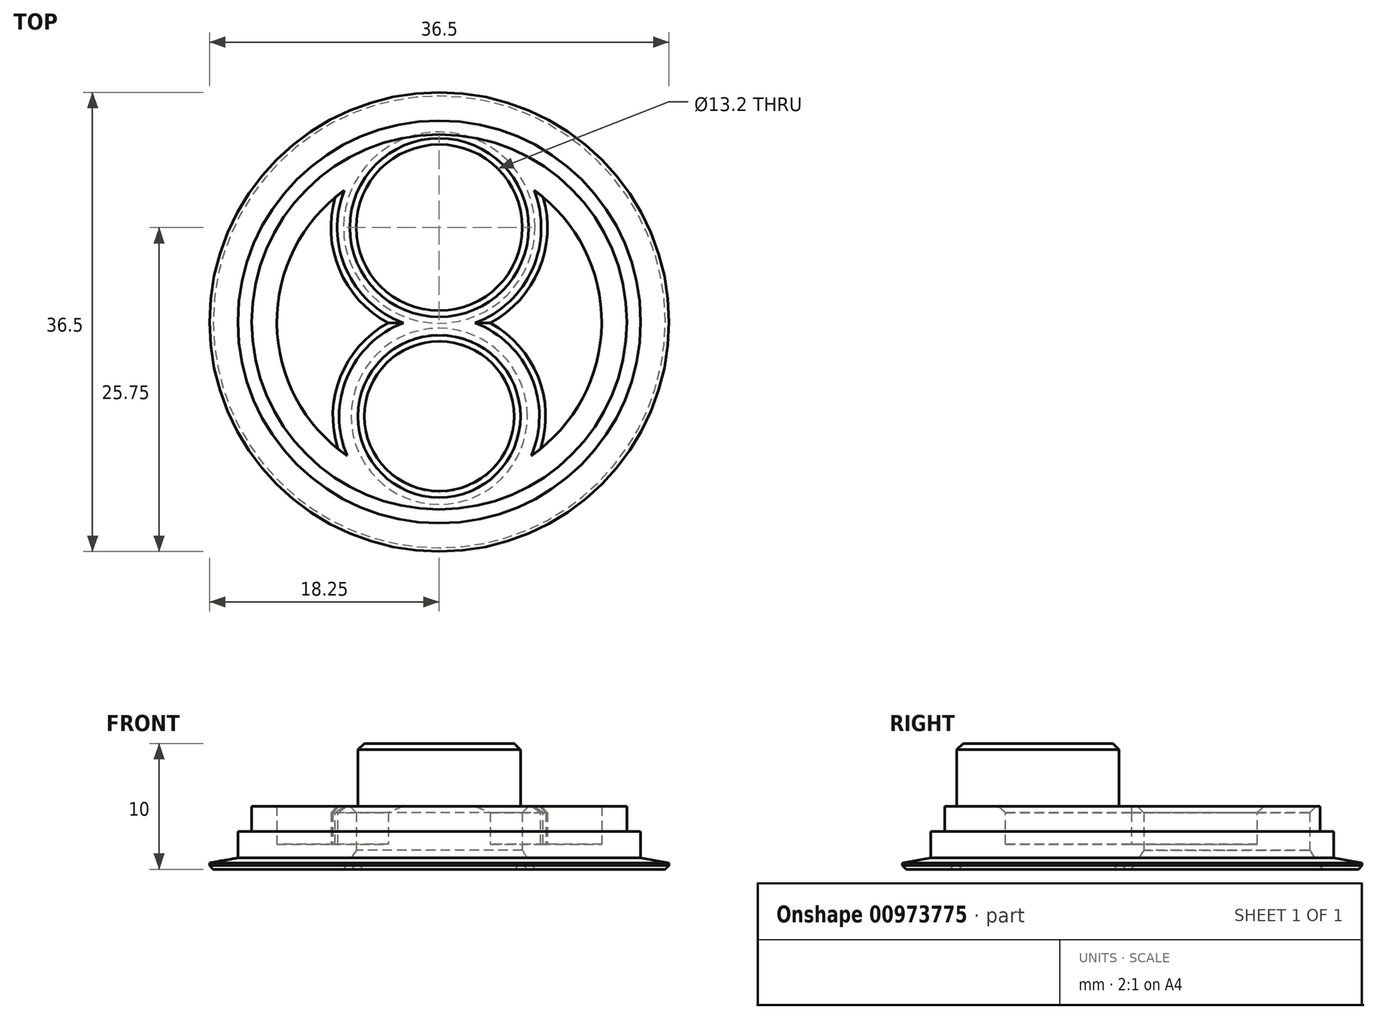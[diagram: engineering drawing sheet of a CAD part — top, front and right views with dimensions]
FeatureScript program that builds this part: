
annotation { "Feature Type Name" : "Feature", "Feature Type Description" : "" }
export const myFeature = defineFeature(function(context is Context, id is Id, definition is map)
    precondition{}
    {
        {
            var Q0;
            Q0=qCreatedBy(makeId("Top.planeOp"),FACE);
            var sketch = newSketch(context, id + "F0", { "sketchPlane" : qUnion([Q0])});
            skCircle(sketch, "E0", {"center": v(0, 0) * mm, "radius": 14.9 * mm});
            skCircle(sketch, "E1", {"center": v(0, 0) * mm, "radius": 18.25 * mm});
            skCircle(sketch, "E2", {"center": v(0, -7.5) * mm, "radius": 6.6 * mm});
            skCircle(sketch, "E3", {"center": v(0, 7.5) * mm, "radius": 6.6 * mm});
            skCircle(sketch, "E4", {"center": v(0, 0) * mm, "radius": 16 * mm});
            skSolve(sketch);
        }
        {
            var Q0;
            Q0=makeQuery(id+"F0.imprint","IMPRINT",FACE,{"disambiguationData":[TD([[makeQuery(id+"F0.imprint","IMPRINT",EDGE,{"derivedFrom":sQuery(id+"F0.wireOp",EDGE,"E0")}),1.0]])]});
            extrude(context, id + "F1", {"entities" : qUnion([Q0]), "depth" : 5 * mm, "offsetDistance" : 25 * mm});
        }
        {
            var Q0;
            Q0=makeQuery(id+"F1.opExtrude","CAP_FACE",FACE,{"disambiguationData":[OSD([sQuery(id+"F0.wireOp",EDGE,"E0"),sQuery(id+"F0.wireOp",EDGE,"E2")])],"isStart":false});
            shell(context, id + "F2", {"entities" : qUnion([Q0]), "thickness" : 2 * mm});
        }
        {
            var Q0;
            Q0=makeQuery(id+"F0.imprint","IMPRINT",FACE,{"disambiguationData":[TD([[makeQuery(id+"F0.imprint","IMPRINT",EDGE,{"derivedFrom":sQuery(id+"F0.wireOp",EDGE,"E0")}),-1.0]])]});
            extrude(context, id + "F3", {"entities" : qUnion([Q0]), "operationType" : NewBodyOperationType.ADD, "depth" : 3 * mm, "offsetDistance" : 25 * mm});
        }
        {
            var Q0;
            Q0 = qSketchRegion(id + "F0", true);
            extrude(context, id + "F4", {"entities" : qUnion([Q0]), "operationType" : NewBodyOperationType.ADD, "depth" : 1 * mm, "offsetDistance" : 25 * mm});
        }
        {
            var Q0;
            Q0=makeQuery(id+"F4.opExtrude","CAP_EDGE",EDGE,{"disambiguationData":[OSD([sQuery(id+"F0.wireOp",EDGE,"E1")])],"isStart":true});
            chamfer(context, id + "F5", {"entities" : qUnion([Q0]), "width" : 0.3 * mm, "tangentPropagation" : true});
        }
        {
            var Q0;
            Q0=makeQuery(id+"F1.opExtrude","SWEPT_FACE",FACE,{"disambiguationData":[OSD([sQuery(id+"F0.wireOp",EDGE,"E3")])]});
            var Q1;
            Q1=makeQuery(id+"F1.opExtrude","CAP_EDGE",EDGE,{"disambiguationData":[OSD([sQuery(id+"F0.wireOp",EDGE,"E2")])],"isStart":false});
            chamfer(context, id + "F6", {"entities" : qUnion([Q0, Q1]), "width" : .5 * mm, "tangentPropagation" : true});
        }
        {
            var Q0;
            Q0=makeQuery(id+"F1.opExtrude","CAP_EDGE",EDGE,{"disambiguationData":[OSD([sQuery(id+"F0.wireOp",EDGE,"E2")])],"isStart":true});
            chamfer(context, id + "F7", {"entities" : qUnion([Q0]), "chamferType" : ChamferType.TWO_OFFSETS, "width1" : 1 * mm, "oppositeDirection" : false, "width2" : 1.5 * mm, "tangentPropagation" : true});
        }
        {
            var Q0;
            Q0=makeQuery(id+"F4.opExtrude","CAP_EDGE",EDGE,{"disambiguationData":[OSD([sQuery(id+"F0.wireOp",EDGE,"E1")])],"isStart":false});
            chamfer(context, id + "F8", {"entities" : qUnion([Q0]), "chamferType" : ChamferType.TWO_OFFSETS, "width1" : 2.8 * mm, "oppositeDirection" : false, "width2" : .5 * mm, "tangentPropagation" : true});
        }
        {
            var Q0;
            Q0=qCreatedBy(makeId("Top.planeOp"),FACE);
            var sketch = newSketch(context, id + "F9", { "sketchPlane" : qUnion([Q0])});
            skCircle(sketch, "E5", {"center": v(0, 0) * mm, "radius": 14.9 * mm});
            skCircle(sketch, "E6", {"center": v(0, 0) * mm, "radius": 18.25 * mm});
            skCircle(sketch, "E7", {"center": v(0, -7.5) * mm, "radius": 6.45 * mm});
            skCircle(sketch, "E8", {"center": v(0, 7.5) * mm, "radius": 6.6 * mm});
            skCircle(sketch, "E9", {"center": v(0, 0) * mm, "radius": 16 * mm});
            skSolve(sketch);
        }
        {
            var Q0;
            Q0=makeQuery(id+"F9.imprint","IMPRINT",FACE,{"disambiguationData":[TD([[makeQuery(id+"F9.imprint","IMPRINT",EDGE,{"derivedFrom":sQuery(id+"F9.wireOp",EDGE,"E5")}),1.0]])]});
            extrude(context, id + "F10", {"entities" : qUnion([Q0]), "depth" : 5 * mm, "offsetDistance" : 25 * mm});
        }
        {
            var Q0;
            Q0=makeQuery(id+"F9.imprint","IMPRINT",FACE,{"disambiguationData":[TD([[makeQuery(id+"F9.imprint","IMPRINT",EDGE,{"derivedFrom":sQuery(id+"F9.wireOp",EDGE,"E5")}),-1.0]])]});
            extrude(context, id + "F11", {"entities" : qUnion([Q0]), "operationType" : NewBodyOperationType.ADD, "depth" : 3 * mm, "offsetDistance" : 25 * mm});
        }
        {
            var Q0;
            Q0=makeQuery(id+"F9.imprint","IMPRINT",FACE,{"disambiguationData":[TD([[makeQuery(id+"F9.imprint","IMPRINT",EDGE,{"derivedFrom":sQuery(id+"F9.wireOp",EDGE,"E6")}),1.0]])]});
            extrude(context, id + "F12", {"entities" : qUnion([Q0]), "operationType" : NewBodyOperationType.ADD, "depth" : 1 * mm, "offsetDistance" : 25 * mm});
        }
        {
            var Q0;
            Q0=makeQuery(id+"F10.opExtrude","CAP_FACE",FACE,{"disambiguationData":[OSD([sQuery(id+"F9.wireOp",EDGE,"E5"),sQuery(id+"F9.wireOp",EDGE,"E7"),sQuery(id+"F9.wireOp",EDGE,"E8")])],"isStart":false});
            shell(context, id + "F13", {"entities" : qUnion([Q0]), "thickness" : 2 * mm});
        }
        {
            var Q0;
            Q0=makeQuery(id+"F9.imprint","IMPRINT",FACE,{"disambiguationData":[TD([[makeQuery(id+"F9.imprint","IMPRINT",EDGE,{"derivedFrom":sQuery(id+"F9.wireOp",EDGE,"E7")}),1.0]])]});
            extrude(context, id + "F14", {"entities" : qUnion([Q0]), "operationType" : NewBodyOperationType.ADD, "depth" : 10 * mm, "offsetDistance" : 25 * mm});
        }
        {
            var Q0;
            Q0=makeQuery(id+"F14.opExtrude","CAP_EDGE",EDGE,{"disambiguationData":[OSD([sQuery(id+"F9.wireOp",EDGE,"E7")])],"isStart":false});
            var Q1;
            Q1=makeQuery(id+"F13.opShell","OFFSET_EDGE",EDGE,{"disambiguationData":[OSD([sQuery(id+"F9.wireOp",EDGE,"E5")]),OD(0.0)]});
            var Q2;
            {var subQ0=sQuery(id+"F9.wireOp",EDGE,"E7");Q2=makeQuery(id+"F13.opShell","OFFSET_EDGE",EDGE,{"disambiguationData":[OSD([subQ0]),TDD([makeQuery(id+"F10.opExtrude","CAP_EDGE",EDGE,{"disambiguationData":[OSD([subQ0])],"isStart":false})]),OD(0.0)]});}
            var Q3;
            {var subQ0=sQuery(id+"F9.wireOp",EDGE,"E8");Q3=makeQuery(id+"F13.opShell","OFFSET_EDGE",EDGE,{"disambiguationData":[OSD([subQ0]),TDD([makeQuery(id+"F10.opExtrude","CAP_EDGE",EDGE,{"disambiguationData":[OSD([subQ0])],"isStart":false})]),OD(0.0)]});}
            var Q4;
            {var subQ0=sQuery(id+"F9.wireOp",EDGE,"E7");Q4=makeQuery(id+"F13.opShell","OFFSET_EDGE",EDGE,{"disambiguationData":[OSD([subQ0]),TDD([makeQuery(id+"F10.opExtrude","CAP_EDGE",EDGE,{"disambiguationData":[OSD([subQ0])],"isStart":false})]),OD(1.0)]});}
            var Q5;
            {var subQ0=sQuery(id+"F9.wireOp",EDGE,"E8");Q5=makeQuery(id+"F13.opShell","OFFSET_EDGE",EDGE,{"disambiguationData":[OSD([subQ0]),TDD([makeQuery(id+"F10.opExtrude","CAP_EDGE",EDGE,{"disambiguationData":[OSD([subQ0])],"isStart":false})]),OD(1.0)]});}
            var Q6;
            Q6=makeQuery(id+"F13.opShell","OFFSET_EDGE",EDGE,{"disambiguationData":[OSD([sQuery(id+"F9.wireOp",EDGE,"E5")]),OD(1.0)]});
            var Q7;
            Q7=makeQuery(id+"F10.opExtrude","CAP_EDGE",EDGE,{"disambiguationData":[OSD([sQuery(id+"F9.wireOp",EDGE,"E5")])],"isStart":false});
            var Q8;
            Q8=makeQuery(id+"F10.opExtrude","CAP_EDGE",EDGE,{"disambiguationData":[OSD([sQuery(id+"F9.wireOp",EDGE,"E8")])],"isStart":false});
            chamfer(context, id + "F15", {"entities" : qUnion([Q0, Q1, Q2, Q3, Q4, Q5, Q6, Q7, Q8]), "width" : 0.5 * mm, "tangentPropagation" : true});
        }
        {
            var Q0;
            {var subQ0=sQuery(id+"F9.wireOp",EDGE,"E7");var subQ1=sQuery(id+"F9.wireOp",EDGE,"E9");var subQ2=sQuery(id+"F9.wireOp",EDGE,"E5");Q0=makeQuery(id+"F14.boolean.opBoolean","MERGE",FACE,{"derivedFrom":[makeQuery(id+"F12.boolean.opBoolean","MERGE",FACE,{"derivedFrom":[makeQuery(id+"F11.boolean.opBoolean","MERGE",FACE,{"derivedFrom":[makeQuery(id+"F10.opExtrude","CAP_FACE",FACE,{"disambiguationData":[OSD([subQ2,subQ0,sQuery(id+"F9.wireOp",EDGE,"E8")])],"isStart":true}),makeQuery(id+"F11.opExtrude","CAP_FACE",FACE,{"disambiguationData":[OSD([subQ2,subQ1])],"isStart":true})]}),makeQuery(id+"F12.opExtrude","CAP_FACE",FACE,{"disambiguationData":[OSD([sQuery(id+"F9.wireOp",EDGE,"E6"),subQ1])],"isStart":true})]}),makeQuery(id+"F14.opExtrude","CAP_FACE",FACE,{"disambiguationData":[OSD([subQ0])],"isStart":true})]});}
            var sketch = newSketch(context, id + "F16", { "sketchPlane" : qUnion([Q0])});
            skCircle(sketch, "E10", {"center": v(0, 7.5) * mm, "radius": 6.5 * mm});
            skSolve(sketch);
        }
        {
            var Q0;
            Q0=qCreatedBy(makeId("Right.planeOp"),FACE);
            var sketch = newSketch(context, id + "F17", { "sketchPlane" : qUnion([Q0])});
            skLineSegment(sketch, "E11", {"start": v(-13.5, 0) * mm, "end": v(-14.5, 0) * mm});
            skLineSegment(sketch, "E12", {"start": v(-14.5, 0) * mm, "end": v(-14, 0.5) * mm});
            skPoint(sketch, "E12.endSnap0", {"position": v(-14, 0) * mm});
            skLineSegment(sketch, "E13", {"start": v(-14, 0.5) * mm, "end": v(-13.5, 0) * mm});
            skSolve(sketch);
        }
        {
            var Q0;
            Q0 = qSketchRegion(id + "F17", true);
            var Q1;
            Q1=sQuery(id+"F16.wireOp",EDGE,"E10");
            sweep(context, id + "F18", {"operationType" : NewBodyOperationType.REMOVE, "profiles" : qUnion([Q0]), "path" : qUnion([Q1])});
        }
        {
            var Q0;
            Q0=makeQuery(id+"F12.opExtrude","CAP_EDGE",EDGE,{"disambiguationData":[OSD([sQuery(id+"F9.wireOp",EDGE,"E6")])],"isStart":false});
            chamfer(context, id + "F19", {"entities" : qUnion([Q0]), "chamferType" : ChamferType.TWO_OFFSETS, "width1" : 2.8 * mm, "oppositeDirection" : false, "width2" : 0.5 * mm, "tangentPropagation" : true});
        }
        {
            var Q0;
            Q0=makeQuery(id+"F12.opExtrude","CAP_EDGE",EDGE,{"disambiguationData":[OSD([sQuery(id+"F9.wireOp",EDGE,"E6")])],"isStart":true});
            chamfer(context, id + "F20", {"entities" : qUnion([Q0]), "width" : 0.3 * mm, "tangentPropagation" : true});
        }
        {
            var Q0;
            Q0=makeQuery(id+"F10.opExtrude","CAP_EDGE",EDGE,{"disambiguationData":[OSD([sQuery(id+"F9.wireOp",EDGE,"E8")])],"isStart":true});
            chamfer(context, id + "F21", {"entities" : qUnion([Q0]), "chamferType" : ChamferType.TWO_OFFSETS, "width1" : 1 * mm, "oppositeDirection" : false, "width2" : 1.5 * mm, "tangentPropagation" : true});
        }
    });
